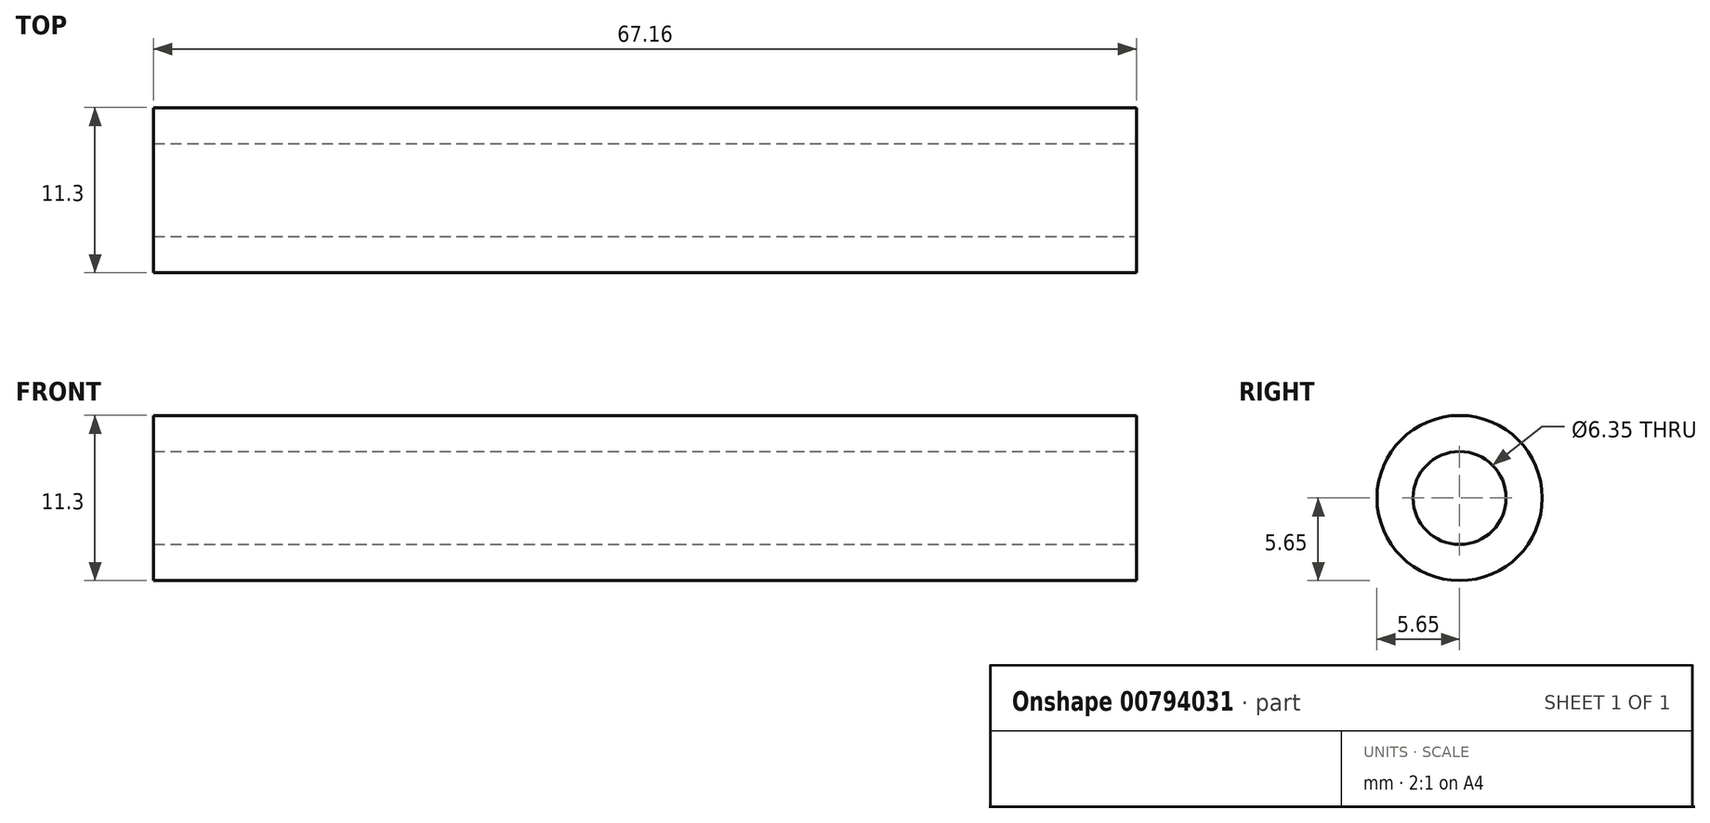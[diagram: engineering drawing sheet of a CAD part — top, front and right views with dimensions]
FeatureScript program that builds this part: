
annotation { "Feature Type Name" : "Feature", "Feature Type Description" : "" }
export const myFeature = defineFeature(function(context is Context, id is Id, definition is map)
    precondition{}
    {
        {
            var Q0;
            Q0=qCreatedBy(makeId("Top.planeOp"),FACE);
            var sketch = newSketch(context, id + "F0", { "sketchPlane" : qUnion([Q0])});
            skLineSegment(sketch, "E0", {"start": v(0, 0) * mm, "end": v(-67.16, 0) * mm});
            skLineSegment(sketch, "E1", {"start": v(-67.16, 0) * mm, "end": v(-67.16, 5.65) * mm});
            skLineSegment(sketch, "E2", {"start": v(-67.16, 5.65) * mm, "end": v(0, 5.65) * mm});
            skLineSegment(sketch, "E3", {"start": v(0, 5.65) * mm, "end": v(0, 0) * mm});
            skSolve(sketch);
        }
        {
            var Q0;
            Q0=qCreatedBy(makeId("Right.planeOp"),FACE);
            var sketch = newSketch(context, id + "F1", { "sketchPlane" : qUnion([Q0])});
            skLineSegment(sketch, "E4", {"start": v(0, 0) * mm, "end": v(4.87, 0) * mm});
            skCircle(sketch, "E5", {"center": v(0, 0) * mm, "radius": 4.87 * mm});
            skSolve(sketch);
        }
        {
            var Q0;
            Q0=makeQuery(id+"F0.imprint","IMPRINT",FACE,{"disambiguationData":[TD([[makeQuery(id+"F0.imprint","IMPRINT",EDGE,{"derivedFrom":sQuery(id+"F0.wireOp",EDGE,"E0")}),-1.0]])]});
            var Q1;
            Q1=sQuery(id+"F0.wireOp",EDGE,"E0");
            revolve(context, id + "F2", {"surfaceOperationType" : NewSurfaceOperationType.NEW, "entities" : qUnion([Q0]), "axis" : qUnion([Q1]), "revolveType" : RevolveType.FULL});
        }
        {
            var Q0;
            Q0=sQuery(id+"F1.wireOp",VERTEX,"E4.start");
            var Q1;
            Q1=makeQuery(id+"F2.opRevolve","SWEPT_BODY",BODY,{"disambiguationData":[OSD([sQuery(id+"F0.wireOp",EDGE,"E0"),sQuery(id+"F0.wireOp",EDGE,"E1"),sQuery(id+"F0.wireOp",EDGE,"E2"),sQuery(id+"F0.wireOp",EDGE,"E3")])]});
            hole(context, id + "F3", {"style" : HoleStyle.SIMPLE, "endStyle" : HoleEndStyle.THROUGH, "holeDiameter" : 6.35 * mm, "majorDiameter" : 6.35 * mm, "isTappedThrough" : true, "tappedDepth" : 12.7 * mm, "tapClearance" : 3, "locations" : qUnion([Q0]), "scope" : qUnion([Q1])});
        }
    });
